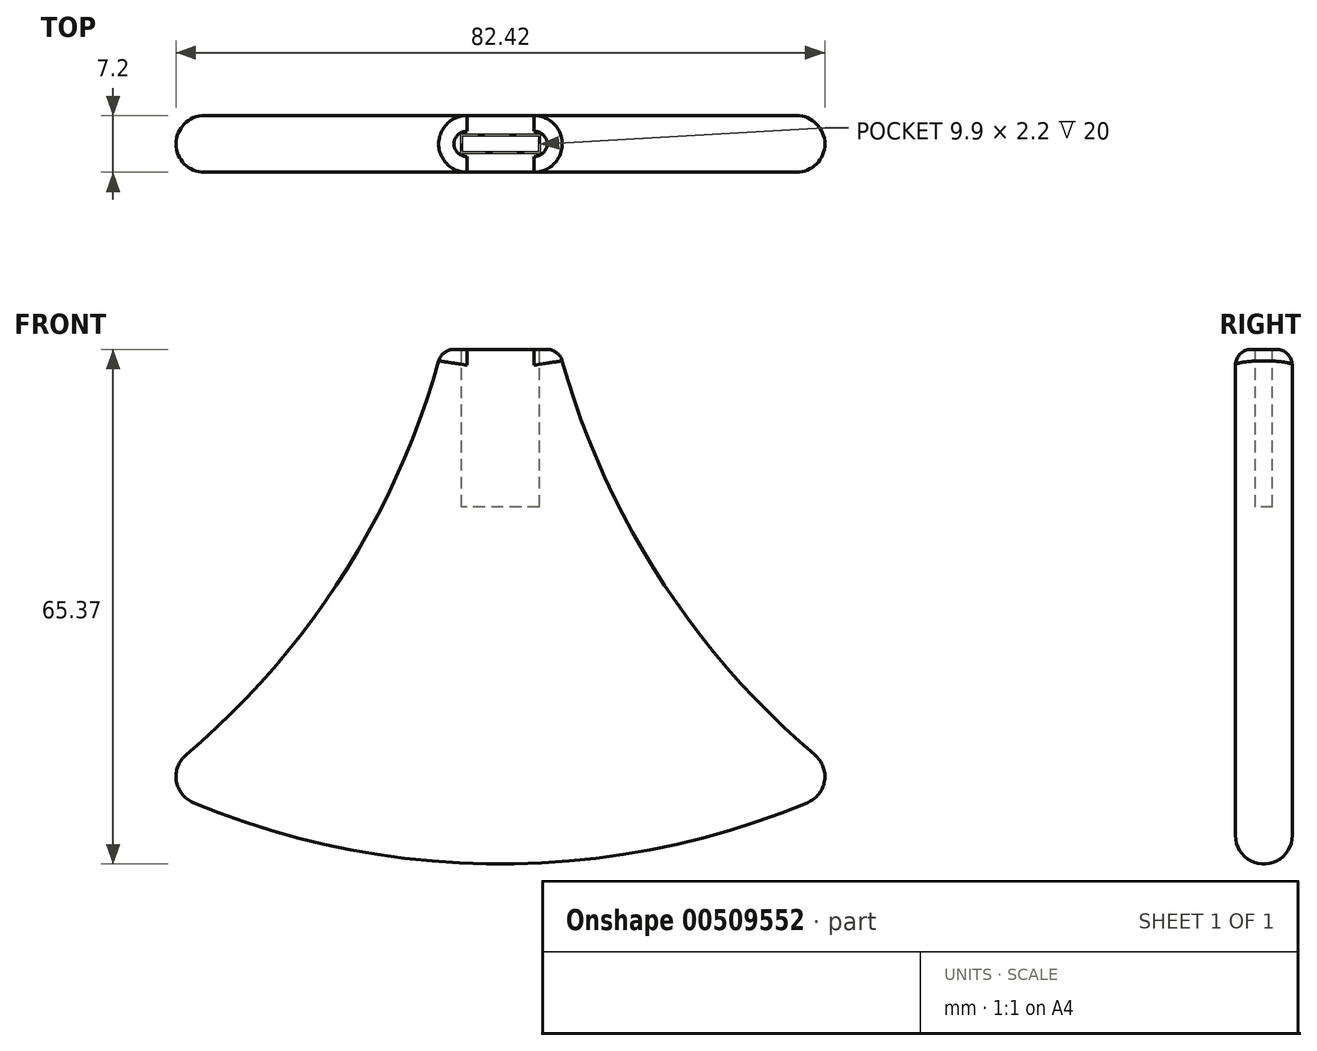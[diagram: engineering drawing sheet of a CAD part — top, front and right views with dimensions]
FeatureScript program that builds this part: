
annotation { "Feature Type Name" : "Feature", "Feature Type Description" : "" }
export const myFeature = defineFeature(function(context is Context, id is Id, definition is map)
    precondition{}
    {
        {
            var Q0;
            Q0=qCreatedBy(makeId("Front.planeOp"),FACE);
            var sketch = newSketch(context, id + "F0", { "sketchPlane" : qUnion([Q0])});
            skArc(sketch, "E0", {"start": v(-44.45, -0.3) * mm, "mid": v(0, -10.53) * mm, "end": v(44.45, -0.3) * mm});
            skLineSegment(sketch, "E1", {"start": v(-7.45, 54.84) * mm, "end": v(7.45, 54.84) * mm});
            skArc(sketch, "E2", {"start": v(-44.45, -0.3) * mm, "mid": v(-21.32, 24.17) * mm, "end": v(-7.45, 54.84) * mm});
            skArc(sketch, "E3", {"start": v(7.45, 54.84) * mm, "mid": v(21.32, 24.17) * mm, "end": v(44.45, -0.3) * mm});
            skSolve(sketch);
        }
        {
            var Q0;
            Q0 = qSketchRegion(id + "F0", true);
            extrude(context, id + "F1", {"entities" : qUnion([Q0]), "endBound" : BoundingType.SYMMETRIC, "depth" : 7.2 * mm});
        }
        {
            var Q0;
            Q0=makeQuery(id+"F1.opExtrude","SWEPT_FACE",FACE,{"disambiguationData":[OSD([sQuery(id+"F0.wireOp",EDGE,"E1")])]});
            var sketch = newSketch(context, id + "F2", { "sketchPlane" : qUnion([Q0])});
            skLineSegment(sketch, "E4.bottom", {"start": v(4.95, 1.1) * mm, "end": v(-4.95, 1.1) * mm});
            skLineSegment(sketch, "E4.top", {"start": v(4.95, -1.1) * mm, "end": v(-4.95, -1.1) * mm});
            skLineSegment(sketch, "E4.left", {"start": v(4.95, 1.1) * mm, "end": v(4.95, -1.1) * mm});
            skLineSegment(sketch, "E4.right", {"start": v(-4.95, 1.1) * mm, "end": v(-4.95, -1.1) * mm});
            skPoint(sketch, "E4.middle", {"position": v(0, 0) * mm});
            skSolve(sketch);
        }
        {
            var Q0;
            Q0=makeQuery(id+"F1.opExtrude","SWEPT_FACE",FACE,{"disambiguationData":[OSD([sQuery(id+"F0.wireOp",EDGE,"E0")])]});
            var Q1;
            Q1=makeQuery(id+"F1.opExtrude","CAP_EDGE",EDGE,{"disambiguationData":[OSD([sQuery(id+"F0.wireOp",EDGE,"E3")])],"isStart":false});
            var Q2;
            Q2=makeQuery(id+"F1.opExtrude","CAP_EDGE",EDGE,{"disambiguationData":[OSD([sQuery(id+"F0.wireOp",EDGE,"E3")])],"isStart":true});
            var Q3;
            Q3=makeQuery(id+"F1.opExtrude","CAP_EDGE",EDGE,{"disambiguationData":[OSD([sQuery(id+"F0.wireOp",EDGE,"E2")])],"isStart":false});
            var Q4;
            Q4=makeQuery(id+"F1.opExtrude","CAP_EDGE",EDGE,{"disambiguationData":[OSD([sQuery(id+"F0.wireOp",EDGE,"E2")])],"isStart":true});
            fillet(context, id + "F3", {"entities" : qUnion([Q0, Q1, Q2, Q3, Q4]), "radius" : 3.6 * mm, "tangentPropagation" : true, "allowEdgeOverflow" : false});
        }
        {
            var Q0;
            Q0=makeQuery(id+"F1.opExtrude","SWEPT_FACE",FACE,{"disambiguationData":[OSD([sQuery(id+"F0.wireOp",EDGE,"E1")])]});
            fillet(context, id + "F4", {"entities" : qUnion([Q0]), "radius" : 2 * mm, "tangentPropagation" : true, "allowEdgeOverflow" : false});
        }
        {
            var Q0;
            Q0=makeQuery(id+"F2.imprint","IMPRINT",FACE,{"disambiguationData":[TD([[makeQuery(id+"F2.imprint","IMPRINT",EDGE,{"derivedFrom":sQuery(id+"F2.wireOp",EDGE,"E4.bottom")}),1.0]])]});
            extrude(context, id + "F5", {"entities" : qUnion([Q0]), "operationType" : NewBodyOperationType.REMOVE, "oppositeDirection" : true, "depth" : 20 * mm});
        }
    });
